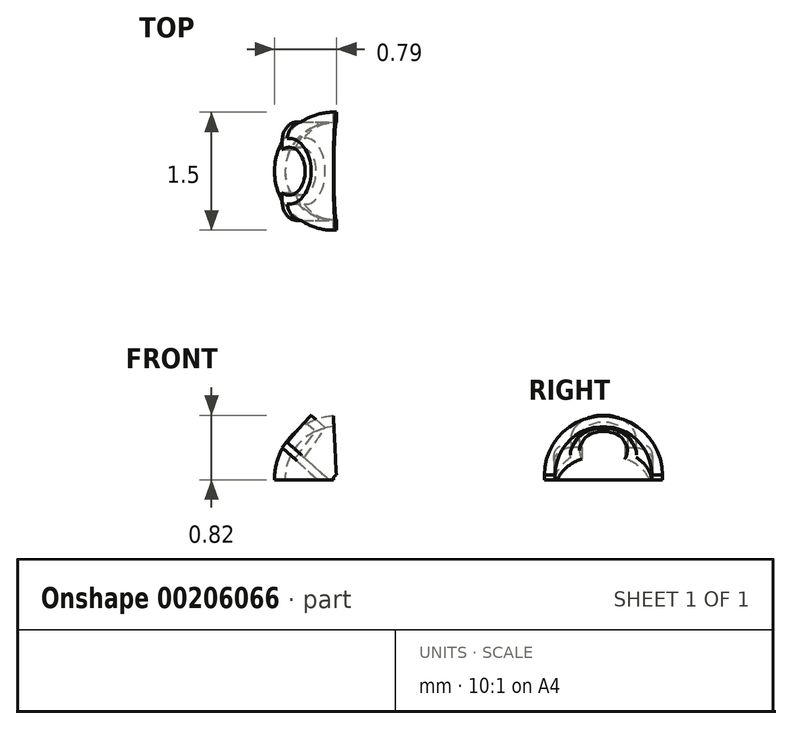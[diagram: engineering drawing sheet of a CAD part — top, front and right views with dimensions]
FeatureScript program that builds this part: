
annotation { "Feature Type Name" : "Feature", "Feature Type Description" : "" }
export const myFeature = defineFeature(function(context is Context, id is Id, definition is map)
    precondition{}
    {
        {
            var Q0;
            Q0=qCreatedBy(makeId("Top.planeOp"),FACE);
            var sketch = newSketch(context, id + "F0", { "sketchPlane" : qUnion([Q0])});
            skLineSegment(sketch, "E0", {"start": v(0, -0.75) * mm, "end": v(0, -0.62) * mm});
            skArc(sketch, "E1", {"start": v(0, 0.75) * mm, "mid": v(-0.75, 0) * mm, "end": v(0, -0.75) * mm});
            skArc(sketch, "E2.0", {"start": v(0, 0.62) * mm, "mid": v(-0.62, 0) * mm, "end": v(0, -0.62) * mm});
            skLineSegment(sketch, "E3.trimOffspring", {"start": v(0, 0.62) * mm, "end": v(0, 0.75) * mm});
            skSolve(sketch);
        }
        {
            var Q0;
            Q0=qCreatedBy(makeId("Front.planeOp"),FACE);
            var sketch = newSketch(context, id + "F1", { "sketchPlane" : qUnion([Q0])});
            skArc(sketch, "E4", {"start": v(0, 0.76) * mm, "mid": v(-0.5, 0.52) * mm, "end": v(-0.7, 0) * mm});
            skSolve(sketch);
        }
        {
            var Q0;
            Q0=qSketchRegion(id+"F0",true);
            var Q1;
            Q1=qConstructionFilter(qBodyType(qCreatedBy(id+"F0",EDGE),BodyType.WIRE),ConstructionObject.NO);
            var Q2;
            Q2=qConstructionFilter(qBodyType(qCreatedBy(id+"F1",EDGE),BodyType.WIRE),ConstructionObject.NO);
            sweep(context, id + "F2", {"profiles" : qUnion([Q0]), "surfaceProfiles" : qUnion([Q1]), "path" : qUnion([Q2])});
        }
        {
            var Q0;
            Q0=makeQuery(id+"F2.opSweep","CAP_FACE",FACE,{"disambiguationData":[OSD([sQuery(id+"F0.wireOp",EDGE,"E0"),sQuery(id+"F0.wireOp",EDGE,"E1"),sQuery(id+"F0.wireOp",EDGE,"E2.0"),sQuery(id+"F0.wireOp",EDGE,"E3.trimOffspring"),sQuery(id+"F1.wireOp",VERTEX,"E4.start")])],"isStart":false});
            var Q1;
            Q1=sQuery(id+"F0.wireOp",EDGE,"E0");
            cPlane(context, id + "F3", {"entities" : qUnion([Q0, Q1]), "cplaneType" : CPlaneType.LINE_ANGLE, "offset" : 25.4 * mm, "angle" : 45 * degree, "width" : 152.4 * mm, "height" : 152.4 * mm});
        }
        {
            var Q0;
            Q0=qCreatedBy(id+"F3.planeOp",FACE);
            var sketch = newSketch(context, id + "F4", { "sketchPlane" : qUnion([Q0])});
            skArc(sketch, "E5", {"start": v(0.27, -0.13) * mm, "mid": v(0, 0.3) * mm, "end": v(-0.27, -0.13) * mm});
            skArc(sketch, "E6", {"start": v(0.41, -0.04) * mm, "mid": v(0, 0.42) * mm, "end": v(-0.41, -0.04) * mm});
            skLineSegment(sketch, "E7", {"start": v(0.27, -0.13) * mm, "end": v(0.63, -0.13) * mm});
            skLineSegment(sketch, "E8", {"start": v(0.63, -0.13) * mm, "end": v(0.63, -0.04) * mm});
            skLineSegment(sketch, "E9", {"start": v(0.63, -0.04) * mm, "end": v(0.41, -0.04) * mm});
            skLineSegment(sketch, "E10", {"start": v(0, 0) * mm, "end": v(0, -0.13) * mm});
            skLineSegment(sketch, "E11.MirrorCS", {"start": v(-0.63, -0.13) * mm, "end": v(-0.63, -0.04) * mm});
            skLineSegment(sketch, "E12.MirrorCS", {"start": v(-0.27, -0.13) * mm, "end": v(-0.63, -0.13) * mm});
            skLineSegment(sketch, "E13.MirrorCS", {"start": v(-0.63, -0.04) * mm, "end": v(-0.41, -0.04) * mm});
            skSolve(sketch);
        }
        {
            var Q0;
            Q0=qSketchRegion(id+"F4",true);
            extrude(context, id + "F5", {"entities" : qUnion([Q0]), "depth" : 0.76 * mm});
        }
        {
            var Q0;
            Q0=makeQuery(id+"F5.opExtrude","CAP_FACE",FACE,{"disambiguationData":[OSD([sQuery(id+"F4.wireOp",EDGE,"E5"),sQuery(id+"F4.wireOp",EDGE,"E6"),sQuery(id+"F4.wireOp",EDGE,"E7"),sQuery(id+"F4.wireOp",EDGE,"E8"),sQuery(id+"F4.wireOp",EDGE,"E9"),sQuery(id+"F4.wireOp",EDGE,"E11.MirrorCS"),sQuery(id+"F4.wireOp",EDGE,"E12.MirrorCS"),sQuery(id+"F4.wireOp",EDGE,"E13.MirrorCS")])],"isStart":true});
            var Q1;
            {var subQ0=sQuery(id+"F0.wireOp",EDGE,"E2.0");Q1=makeQuery(id+"F5.boolean.opBoolean","SPLIT",FACE,{"disambiguationData":[TD([makeQuery(id+"F5.opExtrude","SWEPT_FACE",FACE,{"disambiguationData":[OSD([sQuery(id+"F4.wireOp",EDGE,"E5")])]})])],"derivedFrom":makeQuery(id+"F2.opSweep","SWEPT_FACE",FACE,{"disambiguationData":[OSD([subQ0,sQuery(id+"F1.wireOp",EDGE,"E4")])]})});}
            var Q2;
            Q2=makeQuery(id+"F2.opSweep","SWEPT_BODY",BODY,{"disambiguationData":[OSD([sQuery(id+"F0.wireOp",EDGE,"E0"),sQuery(id+"F0.wireOp",EDGE,"E1"),sQuery(id+"F0.wireOp",EDGE,"E2.0"),sQuery(id+"F0.wireOp",EDGE,"E3.trimOffspring"),sQuery(id+"F1.wireOp",EDGE,"E4")])]});
            extrude(context, id + "F6", {"entities" : qUnion([Q0]), "operationType" : NewBodyOperationType.REMOVE, "endBound" : BoundingType.UP_TO_BODY, "oppositeDirection" : true, "endBoundEntityFace" : qUnion([Q1]), "endBoundEntityBody" : qUnion([Q2]), "depth" : 0.38 * mm});
        }
        {
            var Q0;
            Q0=makeQuery(id+"F5.opExtrude","CAP_EDGE",EDGE,{"disambiguationData":[OSD([sQuery(id+"F4.wireOp",EDGE,"E11.MirrorCS")])],"isStart":false});
            var Q1;
            Q1=makeQuery(id+"F5.opExtrude","CAP_EDGE",EDGE,{"disambiguationData":[OSD([sQuery(id+"F4.wireOp",EDGE,"E8")])],"isStart":false});
            fillet(context, id + "F7", {"entities" : qUnion([Q0, Q1]), "radius" : 0.25 * mm, "tangentPropagation" : true, "allowEdgeOverflow" : false});
        }
    });
